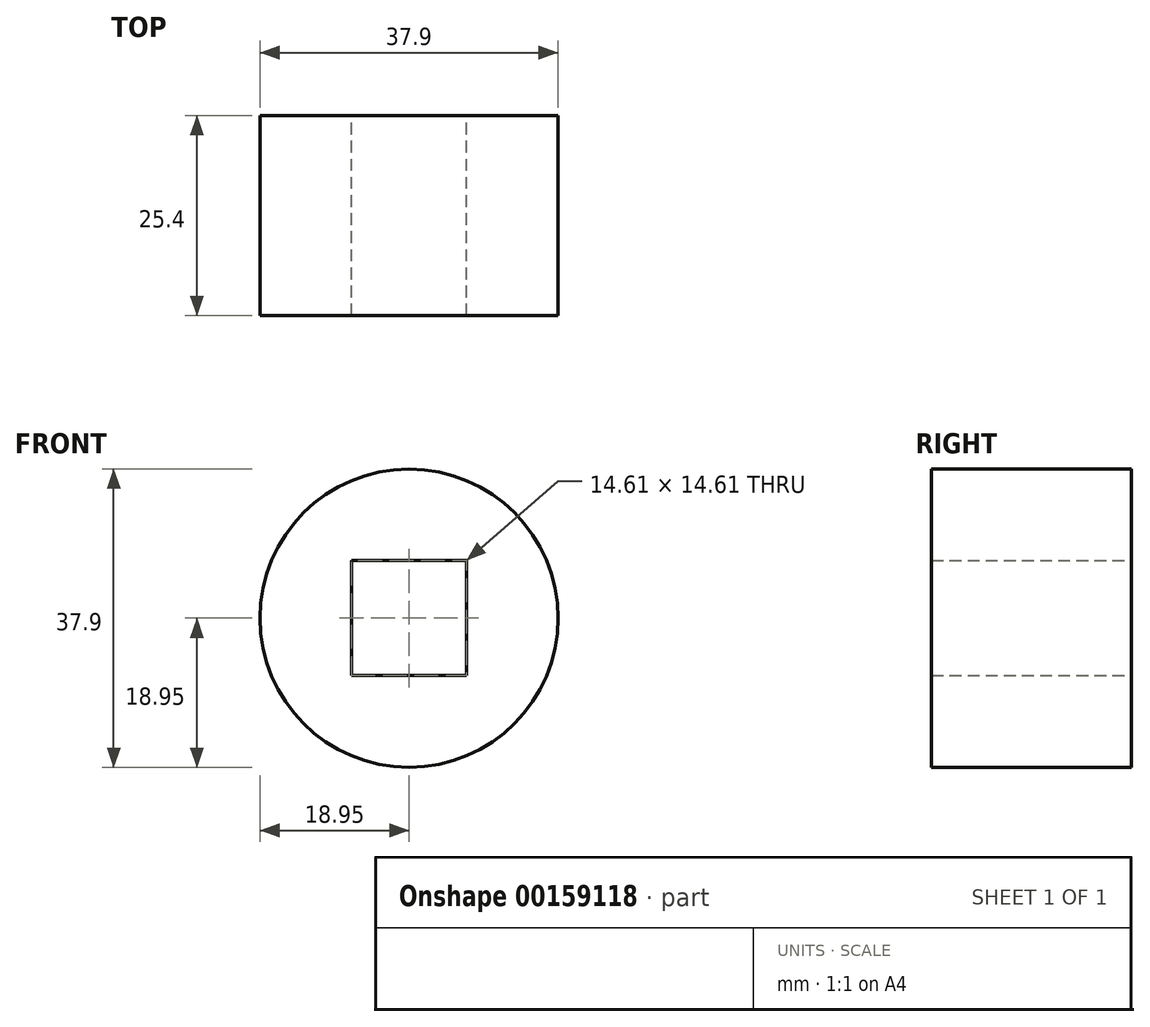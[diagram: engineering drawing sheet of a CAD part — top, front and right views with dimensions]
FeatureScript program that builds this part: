
annotation { "Feature Type Name" : "Feature", "Feature Type Description" : "" }
export const myFeature = defineFeature(function(context is Context, id is Id, definition is map)
    precondition{}
    {
        {
            var Q0;
            Q0=qCreatedBy(makeId("Front.planeOp"),FACE);
            var sketch = newSketch(context, id + "F0", { "sketchPlane" : qUnion([Q0])});
            skCircle(sketch, "E0", {"center": v(0, 0) * mm, "radius": 18.95 * mm});
            skSolve(sketch);
        }
        {
            var Q0;
            Q0=makeQuery(id+"F0.imprint","IMPRINT",FACE,{"disambiguationData":[TD([[makeQuery(id+"F0.imprint","IMPRINT",EDGE,{"derivedFrom":sQuery(id+"F0.wireOp",EDGE,"E0")}),1.0]])]});
            extrude(context, id + "F1", {"entities" : qUnion([Q0]), "depth" : 25.4 * mm});
        }
        {
            var Q0;
            Q0=makeQuery(id+"F1.opExtrude","CAP_FACE",FACE,{"disambiguationData":[OSD([sQuery(id+"F0.wireOp",EDGE,"E0")])],"isStart":true});
            var sketch = newSketch(context, id + "F2", { "sketchPlane" : qUnion([Q0])});
            skLineSegment(sketch, "E1.bottom", {"start": v(7.3, -7.3) * mm, "end": v(-7.3, -7.3) * mm});
            skLineSegment(sketch, "E1.top", {"start": v(7.3, 7.3) * mm, "end": v(-7.3, 7.3) * mm});
            skLineSegment(sketch, "E1.left", {"start": v(7.3, -7.3) * mm, "end": v(7.3, 7.3) * mm});
            skLineSegment(sketch, "E1.right", {"start": v(-7.3, -7.3) * mm, "end": v(-7.3, 7.3) * mm});
            skPoint(sketch, "E1.middle", {"position": v(0, 0) * mm});
            skSolve(sketch);
        }
        {
            var Q0;
            Q0=makeQuery(id+"F2.imprint","IMPRINT",FACE,{"disambiguationData":[TD([[makeQuery(id+"F2.imprint","IMPRINT",EDGE,{"derivedFrom":sQuery(id+"F2.wireOp",EDGE,"E1.bottom")}),-1.0]])]});
            extrude(context, id + "F3", {"entities" : qUnion([Q0]), "operationType" : NewBodyOperationType.REMOVE, "endBound" : BoundingType.THROUGH_ALL, "oppositeDirection" : true, "depth" : 25.4 * mm});
        }
    });
